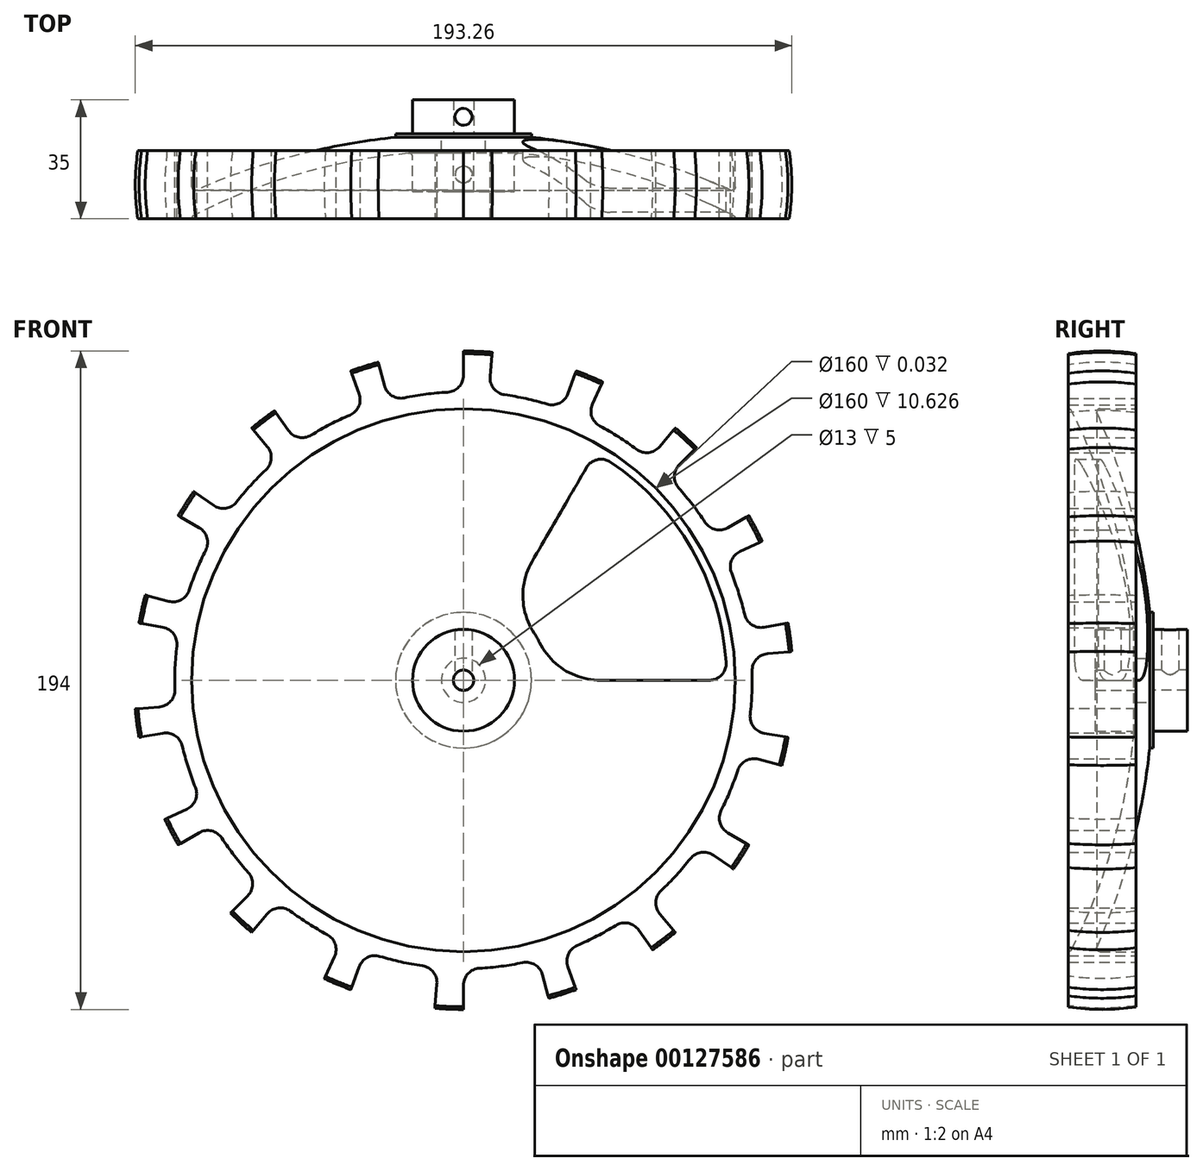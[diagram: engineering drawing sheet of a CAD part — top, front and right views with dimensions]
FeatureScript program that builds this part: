
annotation { "Feature Type Name" : "Feature", "Feature Type Description" : "" }
export const myFeature = defineFeature(function(context is Context, id is Id, definition is map)
    precondition{}
    {
        {
            var Q0;
            Q0=qCreatedBy(makeId("Front.planeOp"),FACE);
            var sketch = newSketch(context, id + "F0", { "sketchPlane" : qUnion([Q0])});
            skCircle(sketch, "E0", {"center": v(0, 0) * mm, "radius": 85 * mm});
            skSolve(sketch);
        }
        {
            var Q0;
            Q0=makeQuery(id+"F0.imprint","IMPRINT",FACE,{"disambiguationData":[TD([[makeQuery(id+"F0.imprint","IMPRINT",EDGE,{"derivedFrom":sQuery(id+"F0.wireOp",EDGE,"E0")}),1.0]])]});
            extrude(context, id + "F1", {"entities" : qUnion([Q0]), "depth" : 25 * mm});
        }
        {
            var Q0;
            Q0=qCreatedBy(makeId("Right.planeOp"),FACE);
            var sketch = newSketch(context, id + "F2", { "sketchPlane" : qUnion([Q0])});
            skCircle(sketch, "E1", {"center": v(-180, 0) * mm, "radius": 175 * mm});
            skLineSegment(sketch, "E2", {"start": v(-378.04, 80) * mm, "end": v(16.3, 80) * mm});
            skLineSegment(sketch, "E3", {"start": v(-5.64, 15) * mm, "end": v(-354.36, 15) * mm});
            skSolve(sketch);
        }
        {
            var Q0;
            {var subQ0=sQuery(id+"F2.wireOp",EDGE,"E2");var subQ1=sQuery(id+"F2.wireOp",EDGE,"E1");var subQ2=makeQuery(id+"F2.imprint","INTERSECT",VERTEX,{"disambiguationData":[OD(0.0)],"derivedFrom":[subQ1,subQ0]});Q0=makeQuery(id+"F2.imprint","IMPRINT",FACE,{"disambiguationData":[TD([[makeQuery(id+"F2.imprint","IMPRINT",EDGE,{"disambiguationData":[TD([[subQ2,1.0]])],"derivedFrom":subQ1}),1.0]])]});}
            var Q1;
            Q1=makeQuery(id+"F1.opExtrude","SWEPT_FACE",FACE,{"disambiguationData":[OSD([sQuery(id+"F0.wireOp",EDGE,"E0")])]});
            revolve(context, id + "F3", {"operationType" : NewBodyOperationType.REMOVE, "entities" : qUnion([Q0]), "axis" : qUnion([Q1]), "revolveType" : RevolveType.FULL, "oppositeDirection" : true});
        }
        {
            var Q0;
            Q0=qCreatedBy(makeId("Right.planeOp"),FACE);
            var sketch = newSketch(context, id + "F4", { "sketchPlane" : qUnion([Q0])});
            skCircle(sketch, "E4", {"center": v(-195, 0) * mm, "radius": 195 * mm});
            skLineSegment(sketch, "E5", {"start": v(-17.17, 80) * mm, "end": v(40, 80) * mm});
            skLineSegment(sketch, "E6", {"start": v(-1.03, 20) * mm, "end": v(40, 20) * mm});
            skLineSegment(sketch, "E7", {"start": v(40, 20) * mm, "end": v(40, 80) * mm});
            skSolve(sketch);
        }
        {
            var Q0;
            {var subQ0=sQuery(id+"F4.wireOp",EDGE,"E5");Q0=makeQuery(id+"F4.imprint","IMPRINT",FACE,{"disambiguationData":[TD([[makeQuery(id+"F4.imprint","IMPRINT",EDGE,{"derivedFrom":subQ0}),-1.0]])]});}
            var Q1;
            Q1=makeQuery(id+"F1.opExtrude","SWEPT_FACE",FACE,{"disambiguationData":[OSD([sQuery(id+"F0.wireOp",EDGE,"E0")])]});
            revolve(context, id + "F5", {"operationType" : NewBodyOperationType.REMOVE, "entities" : qUnion([Q0]), "axis" : qUnion([Q1]), "revolveType" : RevolveType.FULL, "oppositeDirection" : true});
        }
        {
            var Q0;
            {var subQ0=sQuery(id+"F2.wireOp",EDGE,"E2");var subQ1=sQuery(id+"F2.wireOp",EDGE,"E1");Q0=makeQuery(id+"F3.boolean.opBoolean","COPY",EDGE,{"derivedFrom":makeQuery(id+"F3.opRevolve","SWEPT_EDGE",EDGE,{"disambiguationData":[OSD([subQ1,subQ0]),TDD([makeQuery(id+"F2.imprint","INTERSECT",VERTEX,{"disambiguationData":[OD(0.0)],"derivedFrom":[subQ1,subQ0]})])]})});}
            var Q1;
            Q1=makeQuery(id+"F5.boolean.opBoolean","COPY",EDGE,{"derivedFrom":makeQuery(id+"F5.opRevolve","SWEPT_EDGE",EDGE,{"disambiguationData":[OSD([sQuery(id+"F4.wireOp",EDGE,"E4"),sQuery(id+"F4.wireOp",EDGE,"E5")])]})});
            var Q2;
            {var subQ0=sQuery(id+"F2.wireOp",EDGE,"E3");var subQ1=sQuery(id+"F2.wireOp",EDGE,"E1");Q2=makeQuery(id+"F3.boolean.opBoolean","COPY",EDGE,{"derivedFrom":makeQuery(id+"F3.opRevolve","SWEPT_EDGE",EDGE,{"disambiguationData":[OSD([subQ1,subQ0]),TDD([makeQuery(id+"F2.imprint","INTERSECT",VERTEX,{"disambiguationData":[OD(0.0)],"derivedFrom":[subQ1,subQ0]})])]})});}
            fillet(context, id + "F6", {"entities" : qUnion([Q0, Q1, Q2]), "radius" : 1 * mm, "tangentPropagation" : true, "allowEdgeOverflow" : false});
        }
        {
            var Q0;
            Q0=qCreatedBy(makeId("Front.planeOp"),FACE);
            var sketch = newSketch(context, id + "F7", { "sketchPlane" : qUnion([Q0])});
            skCircle(sketch, "E8", {"center": v(0, 0) * mm, "radius": 25 * mm});
            skCircle(sketch, "E9", {"center": v(0, 0) * mm, "radius": 77.5 * mm});
            skLineSegment(sketch, "E10", {"start": v(0, 0) * mm, "end": v(56.09, 97.15) * mm});
            skLineSegment(sketch, "E11", {"start": v(0, 0) * mm, "end": v(100.2, 0) * mm});
            skSolve(sketch);
        }
        {
            var Q0;
            {var subQ0=sQuery(id+"F7.wireOp",EDGE,"E10");var subQ1=sQuery(id+"F7.wireOp",EDGE,"E8");var subQ2=makeQuery(id+"F7.imprint","INTERSECT",VERTEX,{"derivedFrom":[subQ1,subQ0]});Q0=makeQuery(id+"F7.imprint","IMPRINT",FACE,{"disambiguationData":[TD([[makeQuery(id+"F7.imprint","IMPRINT",EDGE,{"disambiguationData":[TD([[subQ2,1.0]])],"derivedFrom":subQ1}),-1.0]])]});}
            extrude(context, id + "F8", {"entities" : qUnion([Q0]), "operationType" : NewBodyOperationType.REMOVE, "depth" : 50 * mm});
        }
        {
            var Q0;
            Q0=makeQuery(id+"F8.boolean.opBoolean","COPY",EDGE,{"derivedFrom":makeQuery(id+"F8.opExtrude","SWEPT_EDGE",EDGE,{"disambiguationData":[OSD([sQuery(id+"F7.wireOp",EDGE,"E9"),sQuery(id+"F7.wireOp",EDGE,"E10")])]})});
            var Q1;
            Q1=makeQuery(id+"F8.boolean.opBoolean","COPY",EDGE,{"derivedFrom":makeQuery(id+"F8.opExtrude","SWEPT_EDGE",EDGE,{"disambiguationData":[OSD([sQuery(id+"F7.wireOp",EDGE,"E9"),sQuery(id+"F7.wireOp",EDGE,"E11")])]})});
            fillet(context, id + "F9", {"entities" : qUnion([Q0, Q1]), "radius" : 5 * mm, "tangentPropagation" : true, "allowEdgeOverflow" : false});
        }
        {
            var Q0;
            Q0=makeQuery(id+"F8.boolean.opBoolean","COPY",EDGE,{"derivedFrom":makeQuery(id+"F8.opExtrude","SWEPT_EDGE",EDGE,{"disambiguationData":[OSD([sQuery(id+"F7.wireOp",EDGE,"E8"),sQuery(id+"F7.wireOp",EDGE,"E10")])]})});
            var Q1;
            Q1=makeQuery(id+"F8.boolean.opBoolean","COPY",EDGE,{"derivedFrom":makeQuery(id+"F8.opExtrude","SWEPT_EDGE",EDGE,{"disambiguationData":[OSD([sQuery(id+"F7.wireOp",EDGE,"E8"),sQuery(id+"F7.wireOp",EDGE,"E11")])]})});
            fillet(context, id + "F10", {"entities" : qUnion([Q0, Q1]), "radius" : 20 * mm, "tangentPropagation" : true, "allowEdgeOverflow" : false});
        }
        {
            var Q0;
            Q0=qCreatedBy(makeId("Right.planeOp"),FACE);
            var sketch = newSketch(context, id + "F11", { "sketchPlane" : qUnion([Q0])});
            skLineSegment(sketch, "E12", {"start": v(0, 0) * mm, "end": v(0, 95.25) * mm});
            skLineSegment(sketch, "E13", {"start": v(-25, 0) * mm, "end": v(-25, 96.23) * mm});
            skLineSegment(sketch, "E14", {"start": v(-25, 84) * mm, "end": v(0, 84) * mm});
            skCircle(sketch, "E15", {"center": v(-15, 32) * mm, "radius": 65 * mm});
            skSolve(sketch);
        }
        {
            var Q0;
            {var subQ3=sQuery(id+"F11.wireOp",EDGE,"E14");Q0=makeQuery(id+"F11.imprint","IMPRINT",FACE,{"disambiguationData":[TD([[makeQuery(id+"F11.imprint","IMPRINT",EDGE,{"derivedFrom":subQ3}),1.0]])]});}
            var Q1;
            Q1=makeQuery(id+"F1.opExtrude","SWEPT_FACE",FACE,{"disambiguationData":[OSD([sQuery(id+"F0.wireOp",EDGE,"E0")])]});
            revolve(context, id + "F12", {"operationType" : NewBodyOperationType.ADD, "entities" : qUnion([Q0]), "axis" : qUnion([Q1]), "revolveType" : RevolveType.ONE_DIRECTION, "angle" : 5 * degree});
        }
        {
            var Q0;
            Q0=makeQuery(id+"F12.boolean.opBoolean","INTERSECT",EDGE,{"derivedFrom":[makeQuery(id+"F1.opExtrude","SWEPT_FACE",FACE,{"disambiguationData":[OSD([sQuery(id+"F0.wireOp",EDGE,"E0")])]}),makeQuery(id+"F12.opRevolve","CAP_FACE",FACE,{"disambiguationData":[OSD([sQuery(id+"F11.wireOp",EDGE,"E12"),sQuery(id+"F11.wireOp",EDGE,"E13"),sQuery(id+"F11.wireOp",EDGE,"E14"),sQuery(id+"F11.wireOp",EDGE,"E15")])],"isStart":true})]});
            var Q1;
            Q1=makeQuery(id+"F12.boolean.opBoolean","INTERSECT",EDGE,{"derivedFrom":[makeQuery(id+"F1.opExtrude","SWEPT_FACE",FACE,{"disambiguationData":[OSD([sQuery(id+"F0.wireOp",EDGE,"E0")])]}),makeQuery(id+"F12.opRevolve","CAP_FACE",FACE,{"disambiguationData":[OSD([sQuery(id+"F11.wireOp",EDGE,"E12"),sQuery(id+"F11.wireOp",EDGE,"E13"),sQuery(id+"F11.wireOp",EDGE,"E14"),sQuery(id+"F11.wireOp",EDGE,"E15")])],"isStart":false})]});
            fillet(context, id + "F13", {"entities" : qUnion([Q0, Q1]), "radius" : 5 * mm, "tangentPropagation" : true, "allowEdgeOverflow" : false});
        }
        {
            var Q0;
            Q0=makeQuery(id+"F12.opRevolve","CAP_FACE",FACE,{"disambiguationData":[OSD([sQuery(id+"F11.wireOp",EDGE,"E12"),sQuery(id+"F11.wireOp",EDGE,"E13"),sQuery(id+"F11.wireOp",EDGE,"E14"),sQuery(id+"F11.wireOp",EDGE,"E15")])],"isStart":false});
            var Q1;
            Q1=makeQuery(id+"F12.opRevolve","SWEPT_FACE",FACE,{"disambiguationData":[OSD([sQuery(id+"F11.wireOp",EDGE,"E15")])]});
            var Q2;
            Q2=makeQuery(id+"F12.opRevolve","CAP_FACE",FACE,{"disambiguationData":[OSD([sQuery(id+"F11.wireOp",EDGE,"E12"),sQuery(id+"F11.wireOp",EDGE,"E13"),sQuery(id+"F11.wireOp",EDGE,"E14"),sQuery(id+"F11.wireOp",EDGE,"E15")])],"isStart":true});
            var Q3;
            {var subQ0=sQuery(id+"F11.wireOp",EDGE,"E15");var subQ1=sQuery(id+"F11.wireOp",EDGE,"E14");var subQ2=sQuery(id+"F11.wireOp",EDGE,"E13");var subQ3=sQuery(id+"F11.wireOp",EDGE,"E12");var subQ4=sQuery(id+"F0.wireOp",EDGE,"E0");Q3=makeQuery(id+"F13.opFillet","BLEND_FACE",FACE,{"disambiguationData":[OSD([subQ4,subQ3,subQ2,subQ1,subQ0]),TDD([makeQuery(id+"F12.boolean.opBoolean","INTERSECT",EDGE,{"derivedFrom":[makeQuery(id+"F1.opExtrude","SWEPT_FACE",FACE,{"disambiguationData":[OSD([subQ4])]}),makeQuery(id+"F12.opRevolve","CAP_FACE",FACE,{"disambiguationData":[OSD([subQ3,subQ2,subQ1,subQ0])],"isStart":false})]})])]});}
            var Q4;
            {var subQ0=sQuery(id+"F11.wireOp",EDGE,"E15");var subQ1=sQuery(id+"F11.wireOp",EDGE,"E14");var subQ2=sQuery(id+"F11.wireOp",EDGE,"E13");var subQ3=sQuery(id+"F11.wireOp",EDGE,"E12");var subQ4=sQuery(id+"F0.wireOp",EDGE,"E0");Q4=makeQuery(id+"F13.opFillet","BLEND_FACE",FACE,{"disambiguationData":[OSD([subQ4,subQ3,subQ2,subQ1,subQ0]),TDD([makeQuery(id+"F12.boolean.opBoolean","INTERSECT",EDGE,{"derivedFrom":[makeQuery(id+"F1.opExtrude","SWEPT_FACE",FACE,{"disambiguationData":[OSD([subQ4])]}),makeQuery(id+"F12.opRevolve","CAP_FACE",FACE,{"disambiguationData":[OSD([subQ3,subQ2,subQ1,subQ0])],"isStart":true})]})])]});}
            var Q5;
            Q5=makeQuery(id+"F3.boolean.opBoolean","COPY",FACE,{"derivedFrom":makeQuery(id+"F3.opRevolve","SWEPT_FACE",FACE,{"disambiguationData":[OSD([sQuery(id+"F2.wireOp",EDGE,"E3")])]})});
            circularPattern(context, id + "F14", {"patternType" : PatternType.FACE, "faces" : qUnion([Q0, Q1, Q2, Q3, Q4]), "axis" : qUnion([Q5]), "angle" : 360 * degree, "instanceCount" : 18, "equalSpace" : true});
        }
        {
            var Q0;
            Q0=qCreatedBy(makeId("Front.planeOp"),FACE);
            var sketch = newSketch(context, id + "F15", { "sketchPlane" : qUnion([Q0])});
            skCircle(sketch, "E16", {"center": v(0, 0) * mm, "radius": 3 * mm});
            skSolve(sketch);
        }
        {
            var Q0;
            Q0=qSketchRegion(id+"F15",true);
            extrude(context, id + "F16", {"entities" : qUnion([Q0]), "operationType" : NewBodyOperationType.REMOVE, "depth" : 25 * mm});
        }
        {
            var Q0;
            Q0=qCreatedBy(makeId("Top.planeOp"),FACE);
            var sketch = newSketch(context, id + "F17", { "sketchPlane" : qUnion([Q0])});
            skCircle(sketch, "E17", {"center": v(0, -12) * mm, "radius": 2.5 * mm});
            skSolve(sketch);
        }
        {
            var Q0;
            Q0=qSketchRegion(id+"F17",true);
            extrude(context, id + "F18", {"entities" : qUnion([Q0]), "operationType" : NewBodyOperationType.REMOVE, "depth" : 25 * mm});
        }
        {
            var Q0;
            Q0=qCreatedBy(makeId("Front.planeOp"),FACE);
            var sketch = newSketch(context, id + "F19", { "sketchPlane" : qUnion([Q0])});
            skCircle(sketch, "E18", {"center": v(0, 0) * mm, "radius": 25 * mm});
            skSolve(sketch);
        }
        {
            var Q0;
            Q0=qSketchRegion(id+"F19",true);
            extrude(context, id + "F20", {"entities" : qUnion([Q0]), "operationType" : NewBodyOperationType.REMOVE, "depth" : 100 * mm, "hasSecondDirection" : true, "secondDirectionOppositeDirection" : false, "secondDirectionDepth" : 17 * mm});
        }
        {
            var Q0;
            Q0=qCreatedBy(makeId("Front.planeOp"),FACE);
            var sketch = newSketch(context, id + "F21", { "sketchPlane" : qUnion([Q0])});
            skCircle(sketch, "E19", {"center": v(0, 0) * mm, "radius": 55 * mm});
            skCircle(sketch, "E20", {"center": v(0, 0) * mm, "radius": 115 * mm});
            skSolve(sketch);
        }
        {
            var Q0;
            Q0=makeQuery(id+"F21.imprint","IMPRINT",FACE,{"disambiguationData":[TD([[makeQuery(id+"F21.imprint","IMPRINT",EDGE,{"derivedFrom":sQuery(id+"F21.wireOp",EDGE,"E19")}),-1.0]])]});
            extrude(context, id + "F22", {"entities" : qUnion([Q0]), "operationType" : NewBodyOperationType.REMOVE, "depth" : 5 * mm});
        }
        {
            var Q0;
            Q0=qCreatedBy(makeId("Front.planeOp"),FACE);
            var sketch = newSketch(context, id + "F23", { "sketchPlane" : qUnion([Q0])});
            skCircle(sketch, "E21", {"center": v(0, 0) * mm, "radius": 6.5 * mm});
            skSolve(sketch);
        }
        {
            var Q0;
            Q0=makeQuery(id+"F23.imprint","IMPRINT",FACE,{"disambiguationData":[TD([[makeQuery(id+"F23.imprint","IMPRINT",EDGE,{"derivedFrom":sQuery(id+"F23.wireOp",EDGE,"E21")}),1.0]])]});
            extrude(context, id + "F24", {"entities" : qUnion([Q0]), "operationType" : NewBodyOperationType.REMOVE, "depth" : 5 * mm});
        }
        {
            var Q0;
            Q0=qCreatedBy(makeId("Front.planeOp"),FACE);
            var sketch = newSketch(context, id + "F25", { "sketchPlane" : qUnion([Q0])});
            skCircle(sketch, "E22", {"center": v(0, 0) * mm, "radius": 15 * mm});
            skCircle(sketch, "E23", {"center": v(0, 0) * mm, "radius": 3 * mm});
            skSolve(sketch);
        }
        {
            var Q0;
            Q0=makeQuery(id+"F25.imprint","IMPRINT",FACE,{"disambiguationData":[TD([[makeQuery(id+"F25.imprint","IMPRINT",EDGE,{"derivedFrom":sQuery(id+"F25.wireOp",EDGE,"E22")}),1.0]])]});
            extrude(context, id + "F26", {"entities" : qUnion([Q0]), "operationType" : NewBodyOperationType.ADD, "oppositeDirection" : true, "depth" : 10 * mm});
        }
        {
            var Q0;
            Q0=qCreatedBy(makeId("Top.planeOp"),FACE);
            var sketch = newSketch(context, id + "F27", { "sketchPlane" : qUnion([Q0])});
            skCircle(sketch, "E24", {"center": v(0, 5) * mm, "radius": 2.5 * mm});
            skSolve(sketch);
        }
        {
            var Q0;
            Q0=qSketchRegion(id+"F27",true);
            extrude(context, id + "F28", {"entities" : qUnion([Q0]), "operationType" : NewBodyOperationType.REMOVE, "depth" : 25 * mm});
        }
    });
